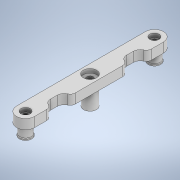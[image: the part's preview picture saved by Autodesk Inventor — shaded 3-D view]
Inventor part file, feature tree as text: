
AUTODESK INVENTOR PART (.ipt)
format: ipt  version: 2022.6 (Build 266554000, 554)  size: 235,520 bytes
history: native  units: mm
features: sketch x10, extrude x7, projected_geometry x7, fillet x4, hole x3, chamfer x1
ambient origin geometry x8: Origin, YZ Plane, XZ Plane, XY Plane, X Axis, Y Axis, Z Axis, Center Point
bodies: Solid1 (feature_tree)
feature tree (32):
  extrude  "Extrusion1"  Depth=7.0mm
  sketch  "Sketch2"  dims[d2=3.75mm d3=0.0mm d11=5.0mm]
  extrude  "Extrusion2"  Depth=3.75mm
  hole  "Hole2"  [1 undecoded]
  hole  "Hole3"  [1 undecoded]
  extrude  "Cut"  TaperAngle=0.0deg  [1 undecoded]
  fillet  "Fillet1"  Radius=2.0mm
  extrude  "Extrusion5"  Depth=3.0mm
  extrude  "Extrusion6"  Depth=3.7mm
  chamfer  "Chamfer1"  Distance=0.8mm
  fillet  "Fillet2"  Radius=0.5mm
  extrude  "Extrusion7"  Depth=10.0mm
  extrude  "Extrusion8"  Depth=10.0mm TaperAngle=0.0deg
  fillet  "Fillet3"  Radius=4.8mm
  fillet  "Fillet4"  Radius=0.4mm
  hole  "Hole4"  [1 undecoded]
  sketch  "Sketch1"  dims[d0=50.0mm d1=7.0mm]
  projected_geometry  "Projected Loop1"
  sketch  "Sketch3"  dims[d12=7.0mm d13=0.0mm d14=2.4mm]
  projected_geometry  "Projected Loop2"
  sketch  "Sketch5"  dims[d18=2.4mm d19=6.0mm d20=4.0mm d21=2.0mm d22=90.0deg d23=10.0mm d24=20.594885mm]
  sketch  "Sketch6"  dims[d25=5.2mm d26=6.0mm d27=4.0mm d28=2.0mm d29=90.0deg d30=1.5mm d31=0.0mm d32=2.5mm]
  sketch  "Sketch8"  dims[d33=5.5mm d35=0.0mm d36=0.0mm d37=2.0mm]
  projected_geometry  "Projected Loop4"
  sketch  "Sketch9"  dims[d38=3.0mm d39=3.0mm]
  projected_geometry  "Projected Loop5"
  sketch  "Sketch10"  dims[d40=5.8mm d41=0.0mm d42=3.7mm]
  sketch  "Sketch11"  dims[d43=3.7mm d44=0.8mm d45=0.0mm]
  projected_geometry  "Projected Loop6"
  projected_geometry  "Projected Loop7"
  sketch  "Sketch13"  dims[d46=0.3mm d47=2.0mm d48=45.0deg d49=0.5mm d50=4.5mm d52=4.0mm d53=0.0mm d54=4.8mm d56=0.4mm d57=0.0mm d61=0.4mm d62=0.8mm d63=2.2mm d64=6.0mm d65=3.6mm d66=1.5mm d67=90.0deg d68=10.0mm d69=20.594885mm d70=4.5mm d71=13.5mm]
  projected_geometry  "Projected Loop10"
note: 4 required parameter values undecoded (feature->parameter linkage not recoverable at this tier; creation-order binding heuristic only, values carry confidence <= 0.55)
